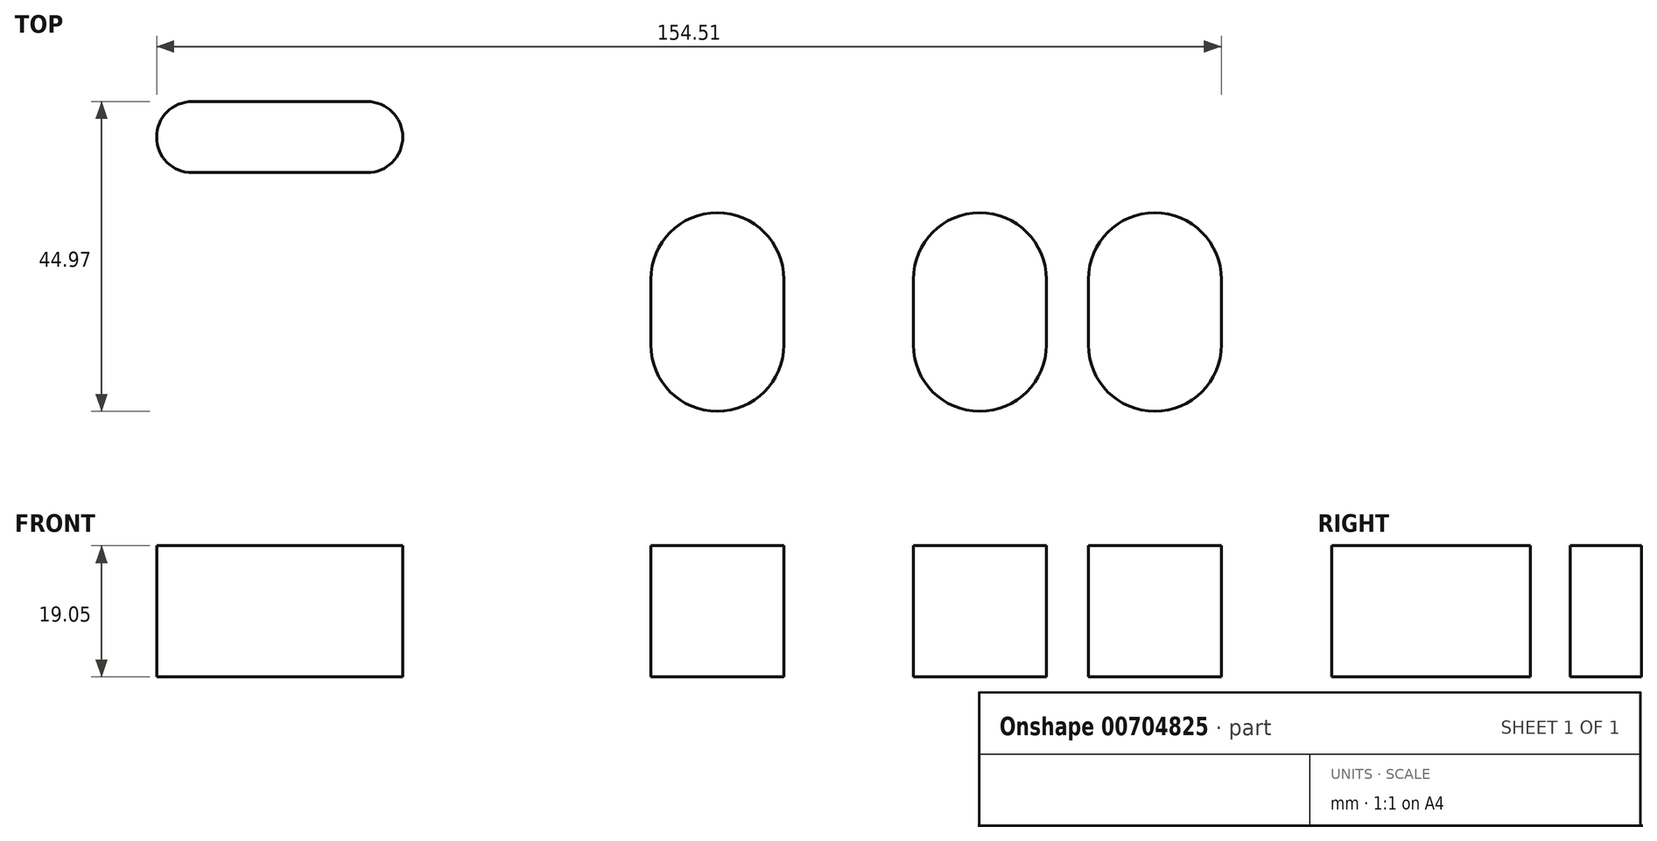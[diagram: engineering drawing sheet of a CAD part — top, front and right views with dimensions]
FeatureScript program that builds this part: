
annotation { "Feature Type Name" : "Feature", "Feature Type Description" : "" }
export const myFeature = defineFeature(function(context is Context, id is Id, definition is map)
    precondition{}
    {
        {
            var Q0;
            Q0=qCreatedBy(makeId("Top.planeOp"),FACE);
            var sketch = newSketch(context, id + "F0", { "sketchPlane" : qUnion([Q0])});
            skLineSegment(sketch, "E0.bottom", {"start": v(82.26, -47.85) * mm, "end": v(-120.94, -47.85) * mm});
            skLineSegment(sketch, "E0.top", {"start": v(82.26, 53.75) * mm, "end": v(-120.94, 53.75) * mm});
            skLineSegment(sketch, "E0.left", {"start": v(82.26, -47.85) * mm, "end": v(82.26, 53.75) * mm});
            skLineSegment(sketch, "E0.right", {"start": v(-120.94, -47.85) * mm, "end": v(-120.94, 53.75) * mm});
            skSolve(sketch);
        }
        {
            var Q0;
            Q0=makeQuery(id+"F0.imprint","IMPRINT",FACE,{"disambiguationData":[TD([[makeQuery(id+"F0.imprint","IMPRINT",EDGE,{"derivedFrom":sQuery(id+"F0.wireOp",EDGE,"E0.bottom")}),-1.0]])]});
            extrude(context, id + "F1", {"entities" : qUnion([Q0]), "depth" : 19.05 * mm, "offsetDistance" : 25.4 * mm});
        }
        {
            var Q0;
            Q0=makeQuery(id+"F1.opExtrude","CAP_FACE",FACE,{"disambiguationData":[OSD([sQuery(id+"F0.wireOp",EDGE,"E0.bottom"),sQuery(id+"F0.wireOp",EDGE,"E0.top"),sQuery(id+"F0.wireOp",EDGE,"E0.left"),sQuery(id+"F0.wireOp",EDGE,"E0.right")])],"isStart":false});
            var sketch = newSketch(context, id + "F2", { "sketchPlane" : qUnion([Q0])});
            skLineSegment(sketch, "E1", {"start": v(-19.34, 53.75) * mm, "end": v(-19.34, -47.85) * mm});
            skLineSegment(sketch, "E2", {"start": v(82.26, 2.95) * mm, "end": v(-120.94, 2.95) * mm});
            skLineSegment(sketch, "E3", {"start": v(-95.54, 28.35) * mm, "end": v(-70.14, 28.35) * mm});
            skArc(sketch, "E4.0.startCap", {"start": v(-95.54, 23.2) * mm, "mid": v(-100.7, 28.35) * mm, "end": v(-95.54, 33.5) * mm});
            skArc(sketch, "E4.0.endCap", {"start": v(-70.14, 33.5) * mm, "mid": v(-64.98, 28.35) * mm, "end": v(-70.14, 23.2) * mm});
            skLineSegment(sketch, "E4.0.left", {"start": v(-95.54, 33.5) * mm, "end": v(-70.14, 33.5) * mm});
            skLineSegment(sketch, "E4.0.right", {"start": v(-95.54, 23.2) * mm, "end": v(-70.14, 23.2) * mm});
            skArc(sketch, "E5.MirrorCS", {"start": v(31.46, 33.5) * mm, "mid": v(26.3, 28.35) * mm, "end": v(31.46, 23.2) * mm});
            skLineSegment(sketch, "E6.MirrorCS", {"start": v(56.86, 33.5) * mm, "end": v(31.46, 33.5) * mm});
            skArc(sketch, "E7.MirrorCS", {"start": v(56.86, 23.2) * mm, "mid": v(62.02, 28.35) * mm, "end": v(56.86, 33.5) * mm});
            skLineSegment(sketch, "E8.MirrorCS", {"start": v(56.86, 23.2) * mm, "end": v(31.46, 23.2) * mm});
            skArc(sketch, "E9.MirrorCS", {"start": v(-95.54, -17.3) * mm, "mid": v(-100.7, -22.45) * mm, "end": v(-95.54, -27.6) * mm});
            skLineSegment(sketch, "E10.MirrorCS", {"start": v(-95.54, -27.6) * mm, "end": v(-70.14, -27.6) * mm});
            skArc(sketch, "E11.MirrorCS", {"start": v(-70.14, -27.6) * mm, "mid": v(-64.98, -22.45) * mm, "end": v(-70.14, -17.3) * mm});
            skLineSegment(sketch, "E12.MirrorCS", {"start": v(-95.54, -17.3) * mm, "end": v(-70.14, -17.3) * mm});
            skLineSegment(sketch, "E13.MirrorCS", {"start": v(56.86, -27.6) * mm, "end": v(31.46, -27.6) * mm});
            skArc(sketch, "E14.MirrorCS", {"start": v(56.86, -17.3) * mm, "mid": v(62.02, -22.45) * mm, "end": v(56.86, -27.6) * mm});
            skLineSegment(sketch, "E15.MirrorCS", {"start": v(56.86, -17.3) * mm, "end": v(31.46, -17.3) * mm});
            skArc(sketch, "E16.MirrorCS", {"start": v(31.46, -27.6) * mm, "mid": v(26.3, -22.45) * mm, "end": v(31.46, -17.3) * mm});
            skArc(sketch, "E17.0.startCap", {"start": v(-95.54, 20.41) * mm, "mid": v(-103.48, 28.35) * mm, "end": v(-95.54, 36.29) * mm});
            skArc(sketch, "E17.0.endCap", {"start": v(-70.14, 36.29) * mm, "mid": v(-62.2, 28.35) * mm, "end": v(-70.14, 20.41) * mm});
            skLineSegment(sketch, "E17.0.left", {"start": v(-95.54, 36.29) * mm, "end": v(-70.14, 36.29) * mm});
            skLineSegment(sketch, "E17.0.right", {"start": v(-95.54, 20.41) * mm, "end": v(-70.14, 20.41) * mm});
            skArc(sketch, "E18.MirrorCS", {"start": v(31.46, 36.29) * mm, "mid": v(23.52, 28.35) * mm, "end": v(31.46, 20.41) * mm});
            skLineSegment(sketch, "E19.MirrorCS", {"start": v(56.86, 36.29) * mm, "end": v(31.46, 36.29) * mm});
            skArc(sketch, "E20.MirrorCS", {"start": v(56.86, 20.41) * mm, "mid": v(64.8, 28.35) * mm, "end": v(56.86, 36.29) * mm});
            skLineSegment(sketch, "E21.MirrorCS", {"start": v(56.86, 20.41) * mm, "end": v(31.46, 20.41) * mm});
            skArc(sketch, "E22.MirrorCS", {"start": v(-70.14, -30.39) * mm, "mid": v(-62.2, -22.45) * mm, "end": v(-70.14, -14.51) * mm});
            skLineSegment(sketch, "E23.MirrorCS", {"start": v(-95.54, -30.39) * mm, "end": v(-70.14, -30.39) * mm});
            skArc(sketch, "E24.MirrorCS", {"start": v(-95.54, -14.51) * mm, "mid": v(-103.48, -22.45) * mm, "end": v(-95.54, -30.39) * mm});
            skLineSegment(sketch, "E25.MirrorCS", {"start": v(-95.54, -14.51) * mm, "end": v(-70.14, -14.51) * mm});
            skLineSegment(sketch, "E26.MirrorCS", {"start": v(56.86, -30.39) * mm, "end": v(31.46, -30.39) * mm});
            skArc(sketch, "E27.MirrorCS", {"start": v(31.46, -30.39) * mm, "mid": v(23.52, -22.45) * mm, "end": v(31.46, -14.51) * mm});
            skArc(sketch, "E28.MirrorCS", {"start": v(56.86, -14.51) * mm, "mid": v(64.8, -22.45) * mm, "end": v(56.86, -30.39) * mm});
            skLineSegment(sketch, "E29.MirrorCS", {"start": v(56.86, -14.51) * mm, "end": v(31.46, -14.51) * mm});
            skSolve(sketch);
        }
        {
            var Q0;
            Q0=makeQuery(id+"F2.imprint","IMPRINT",FACE,{"disambiguationData":[TD([[makeQuery(id+"F2.imprint","IMPRINT",EDGE,{"derivedFrom":sQuery(id+"F2.wireOp",EDGE,"E4.0.startCap")}),-1.0]])]});
            var Q1;
            Q1=makeQuery(id+"F2.imprint","IMPRINT",FACE,{"disambiguationData":[TD([[makeQuery(id+"F2.imprint","IMPRINT",EDGE,{"derivedFrom":sQuery(id+"F2.wireOp",EDGE,"E5.MirrorCS")}),1.0]])]});
            var Q2;
            Q2=makeQuery(id+"F2.imprint","IMPRINT",FACE,{"disambiguationData":[TD([[makeQuery(id+"F2.imprint","IMPRINT",EDGE,{"derivedFrom":sQuery(id+"F2.wireOp",EDGE,"E13.MirrorCS")}),-1.0]])]});
            var Q3;
            Q3=makeQuery(id+"F2.imprint","IMPRINT",FACE,{"disambiguationData":[TD([[makeQuery(id+"F2.imprint","IMPRINT",EDGE,{"derivedFrom":sQuery(id+"F2.wireOp",EDGE,"E9.MirrorCS")}),1.0]])]});
            extrude(context, id + "F3", {"entities" : qUnion([Q0, Q1, Q2, Q3]), "operationType" : NewBodyOperationType.REMOVE, "endBound" : BoundingType.THROUGH_ALL, "oppositeDirection" : true, "depth" : 25.4 * mm, "offsetDistance" : 25.4 * mm});
        }
        {
            var Q0;
            Q0=qSketchRegion(id+"F2",true);
            extrude(context, id + "F4", {"entities" : qUnion([Q0]), "operationType" : NewBodyOperationType.REMOVE, "oppositeDirection" : true, "depth" : 9.52 * mm, "offsetDistance" : 25.4 * mm});
        }
        {
            var Q0;
            Q0=makeQuery(id+"F1.opExtrude","CAP_FACE",FACE,{"disambiguationData":[OSD([sQuery(id+"F0.wireOp",EDGE,"E0.bottom"),sQuery(id+"F0.wireOp",EDGE,"E0.top"),sQuery(id+"F0.wireOp",EDGE,"E0.left"),sQuery(id+"F0.wireOp",EDGE,"E0.right")])],"isStart":false});
            var sketch = newSketch(context, id + "F5", { "sketchPlane" : qUnion([Q0])});
            skPoint(sketch, "E30", {"position": v(-19.34, 2.32) * mm});
            skLineSegment(sketch, "E31", {"start": v(-120.94, 2.95) * mm, "end": v(82.26, 2.95) * mm});
            skLineSegment(sketch, "E32", {"start": v(-19.34, 2.95) * mm, "end": v(-19.34, -1.81) * mm});
            skLineSegment(sketch, "E33.MirrorCS", {"start": v(-19.34, 2.95) * mm, "end": v(-19.34, 7.71) * mm});
            skLineSegment(sketch, "E34", {"start": v(-19.34, 7.71) * mm, "end": v(-19.34, -1.81) * mm});
            skArc(sketch, "E35.0.startCap", {"start": v(-29, 7.71) * mm, "mid": v(-19.34, 17.37) * mm, "end": v(-9.69, 7.71) * mm});
            skArc(sketch, "E35.0.endCap", {"start": v(-9.69, -1.81) * mm, "mid": v(-19.34, -11.46) * mm, "end": v(-29, -1.81) * mm});
            skLineSegment(sketch, "E35.0.left", {"start": v(-9.69, 7.71) * mm, "end": v(-9.69, -1.81) * mm});
            skLineSegment(sketch, "E35.0.right", {"start": v(-29, 7.71) * mm, "end": v(-29, -1.81) * mm});
            skLineSegment(sketch, "E36.0", {"start": v(18.76, 7.71) * mm, "end": v(18.76, -1.81) * mm});
            skLineSegment(sketch, "E37.0", {"start": v(44.16, 7.71) * mm, "end": v(44.16, -1.81) * mm});
            skLineSegment(sketch, "E38.0", {"start": v(88.61, -54.2) * mm, "end": v(88.61, 60.1) * mm});
            skLineSegment(sketch, "E38.1", {"start": v(-127.29, -54.2) * mm, "end": v(88.61, -54.2) * mm});
            skLineSegment(sketch, "E38.2", {"start": v(-127.29, 60.1) * mm, "end": v(-127.29, -54.2) * mm});
            skLineSegment(sketch, "E38.3", {"start": v(88.61, 60.1) * mm, "end": v(-127.29, 60.1) * mm});
            skArc(sketch, "E39.0.startCap", {"start": v(9.1, 7.71) * mm, "mid": v(18.76, 17.37) * mm, "end": v(28.41, 7.71) * mm});
            skArc(sketch, "E39.0.endCap", {"start": v(28.41, -1.81) * mm, "mid": v(18.76, -11.46) * mm, "end": v(9.1, -1.81) * mm});
            skLineSegment(sketch, "E39.0.left", {"start": v(28.41, 7.71) * mm, "end": v(28.41, -1.81) * mm});
            skLineSegment(sketch, "E39.0.right", {"start": v(9.1, 7.71) * mm, "end": v(9.1, -1.81) * mm});
            skArc(sketch, "E39.1.startCap", {"start": v(34.5, 7.71) * mm, "mid": v(44.16, 17.37) * mm, "end": v(53.81, 7.71) * mm});
            skArc(sketch, "E39.1.endCap", {"start": v(53.81, -1.81) * mm, "mid": v(44.16, -11.46) * mm, "end": v(34.5, -1.81) * mm});
            skLineSegment(sketch, "E39.1.left", {"start": v(53.81, 7.71) * mm, "end": v(53.81, -1.81) * mm});
            skLineSegment(sketch, "E39.1.right", {"start": v(34.5, 7.71) * mm, "end": v(34.5, -1.81) * mm});
            skSolve(sketch);
        }
        {
            var Q0;
            {var subQ0=sQuery(id+"F5.wireOp",EDGE,"E35.0.startCap");Q0=makeQuery(id+"F5.imprint","IMPRINT",FACE,{"disambiguationData":[TD([[makeQuery(id+"F5.imprint","IMPRINT",EDGE,{"derivedFrom":subQ0}),-1.0]])]});}
            var Q1;
            {var subQ1=sQuery(id+"F5.wireOp",EDGE,"E35.0.endCap");Q1=makeQuery(id+"F5.imprint","IMPRINT",FACE,{"disambiguationData":[TD([[makeQuery(id+"F5.imprint","IMPRINT",EDGE,{"derivedFrom":subQ1}),-1.0]])]});}
            var Q2;
            {var subQ1=sQuery(id+"F5.wireOp",EDGE,"E39.0.startCap");Q2=makeQuery(id+"F5.imprint","IMPRINT",FACE,{"disambiguationData":[TD([[makeQuery(id+"F5.imprint","IMPRINT",EDGE,{"derivedFrom":subQ1}),-1.0]])]});}
            var Q3;
            {var subQ1=sQuery(id+"F5.wireOp",EDGE,"E39.0.endCap");Q3=makeQuery(id+"F5.imprint","IMPRINT",FACE,{"disambiguationData":[TD([[makeQuery(id+"F5.imprint","IMPRINT",EDGE,{"derivedFrom":subQ1}),-1.0]])]});}
            var Q4;
            {var subQ0=sQuery(id+"F5.wireOp",EDGE,"E39.1.startCap");Q4=makeQuery(id+"F5.imprint","IMPRINT",FACE,{"disambiguationData":[TD([[makeQuery(id+"F5.imprint","IMPRINT",EDGE,{"derivedFrom":subQ0}),-1.0]])]});}
            var Q5;
            {var subQ1=sQuery(id+"F5.wireOp",EDGE,"E39.1.endCap");Q5=makeQuery(id+"F5.imprint","IMPRINT",FACE,{"disambiguationData":[TD([[makeQuery(id+"F5.imprint","IMPRINT",EDGE,{"derivedFrom":subQ1}),-1.0]])]});}
            extrude(context, id + "F6", {"entities" : qUnion([Q0, Q1, Q2, Q3, Q4, Q5]), "operationType" : NewBodyOperationType.REMOVE, "endBound" : BoundingType.THROUGH_ALL, "oppositeDirection" : true, "depth" : 25.4 * mm, "offsetDistance" : 25.4 * mm});
        }
    });
